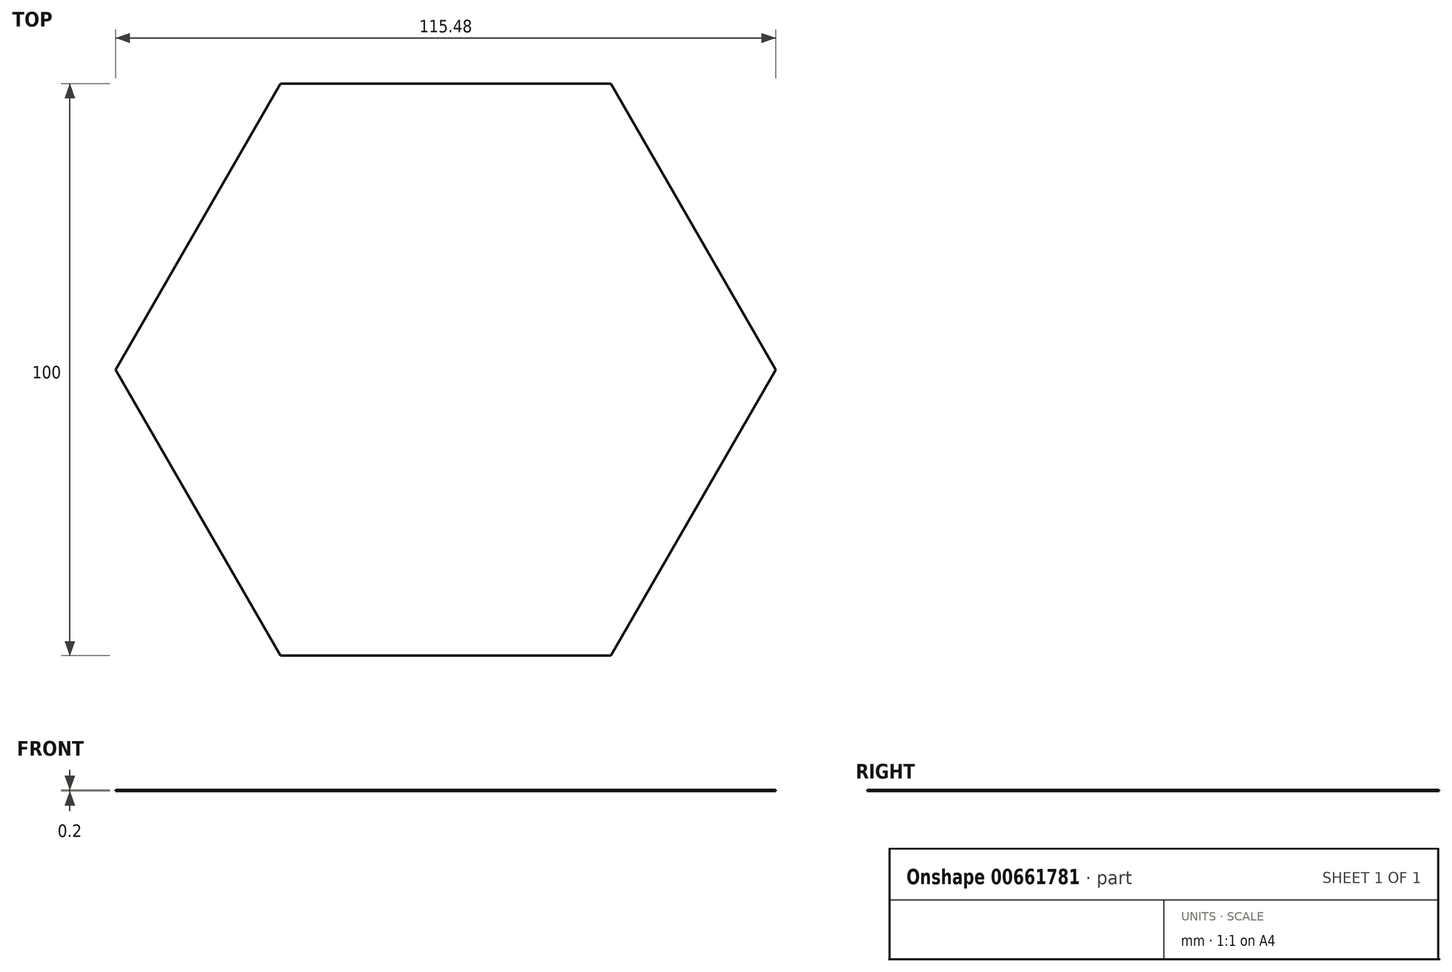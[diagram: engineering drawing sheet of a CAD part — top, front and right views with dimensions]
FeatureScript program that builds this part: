
annotation { "Feature Type Name" : "Feature", "Feature Type Description" : "" }
export const myFeature = defineFeature(function(context is Context, id is Id, definition is map)
    precondition{}
    {
        {
            var Q0;
            Q0=qCreatedBy(makeId("Top.planeOp"),FACE);
            var sketch = newSketch(context, id + "F0", { "sketchPlane" : qUnion([Q0])});
            skCircle(sketch, "E0.cCircle", {"center": v(0, 0) * mm, "radius": 50 * mm, "construction": true});
            skLineSegment(sketch, "E0.0", {"start": v(28.87, -50) * mm, "end": v(-28.87, -50) * mm});
            skLineSegment(sketch, "E0.1", {"start": v(-28.87, -50) * mm, "end": v(-57.74, 0) * mm});
            skLineSegment(sketch, "E0.2", {"start": v(-57.74, 0) * mm, "end": v(-28.87, 50) * mm});
            skLineSegment(sketch, "E0.3", {"start": v(-28.87, 50) * mm, "end": v(28.87, 50) * mm});
            skLineSegment(sketch, "E0.4", {"start": v(28.87, 50) * mm, "end": v(57.74, 0) * mm});
            skLineSegment(sketch, "E0.5", {"start": v(57.74, 0) * mm, "end": v(28.87, -50) * mm});
            skPoint(sketch, "E0.0.midPoint", {"position": v(0, -50) * mm});
            skSolve(sketch);
        }
        {
            var Q0;
            Q0=makeQuery(id+"F0.imprint","IMPRINT",FACE,{"disambiguationData":[TD([[makeQuery(id+"F0.imprint","IMPRINT",EDGE,{"derivedFrom":sQuery(id+"F0.wireOp",EDGE,"E0.0")}),-1.0]])]});
            extrude(context, id + "F1", {"entities" : qUnion([Q0]), "depth" : 0.2 * mm, "offsetDistance" : 25 * mm});
        }
    });
